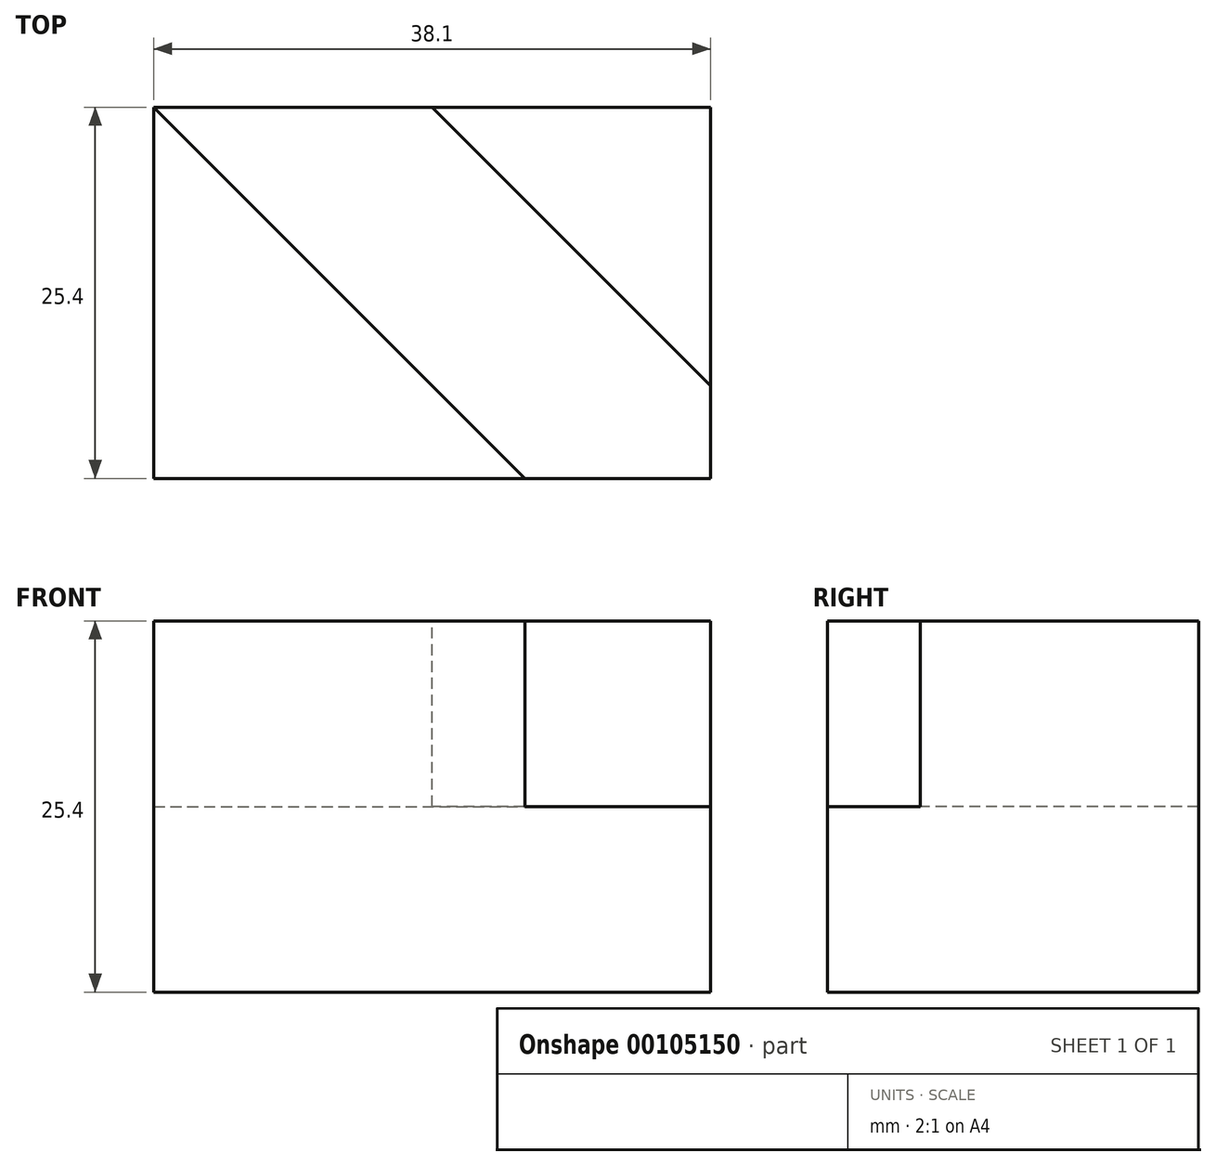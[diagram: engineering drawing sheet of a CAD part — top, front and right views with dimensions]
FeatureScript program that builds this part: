
annotation { "Feature Type Name" : "Feature", "Feature Type Description" : "" }
export const myFeature = defineFeature(function(context is Context, id is Id, definition is map)
    precondition{}
    {
        {
            var Q0;
            Q0=qCreatedBy(makeId("Front.planeOp"),FACE);
            var sketch = newSketch(context, id + "F0", { "sketchPlane" : qUnion([Q0])});
            skLineSegment(sketch, "E0.bottom", {"start": v(0, 0) * mm, "end": v(38.1, 0) * mm});
            skLineSegment(sketch, "E0.top", {"start": v(0, 25.4) * mm, "end": v(38.1, 25.4) * mm});
            skLineSegment(sketch, "E0.left", {"start": v(0, 0) * mm, "end": v(0, 25.4) * mm});
            skLineSegment(sketch, "E0.right", {"start": v(38.1, 0) * mm, "end": v(38.1, 25.4) * mm});
            skSolve(sketch);
        }
        {
            var Q0;
            Q0 = qSketchRegion(id + "F0", true);
            extrude(context, id + "F1", {"entities" : qUnion([Q0]), "depth" : 25.4 * mm});
        }
        {
            var Q0;
            Q0=makeQuery(id+"F1.opExtrude","SWEPT_FACE",FACE,{"disambiguationData":[OSD([sQuery(id+"F0.wireOp",EDGE,"E0.top")])]});
            var sketch = newSketch(context, id + "F2", { "sketchPlane" : qUnion([Q0])});
            skLineSegment(sketch, "E1", {"start": v(0, 0) * mm, "end": v(25.4, -25.4) * mm});
            skLineSegment(sketch, "E2", {"start": v(25.4, -25.4) * mm, "end": v(38.1, -25.4) * mm});
            skLineSegment(sketch, "E3", {"start": v(38.1, -25.4) * mm, "end": v(38.1, -19.05) * mm});
            skLineSegment(sketch, "E4", {"start": v(38.1, -19.05) * mm, "end": v(19.05, 0) * mm});
            skLineSegment(sketch, "E5", {"start": v(19.05, 0) * mm, "end": v(0, 0) * mm});
            skSolve(sketch);
        }
        {
            var Q0;
            Q0 = qSketchRegion(id + "F2", true);
            extrude(context, id + "F3", {"entities" : qUnion([Q0]), "operationType" : NewBodyOperationType.REMOVE, "oppositeDirection" : true, "depth" : 12.7 * mm});
        }
    });
